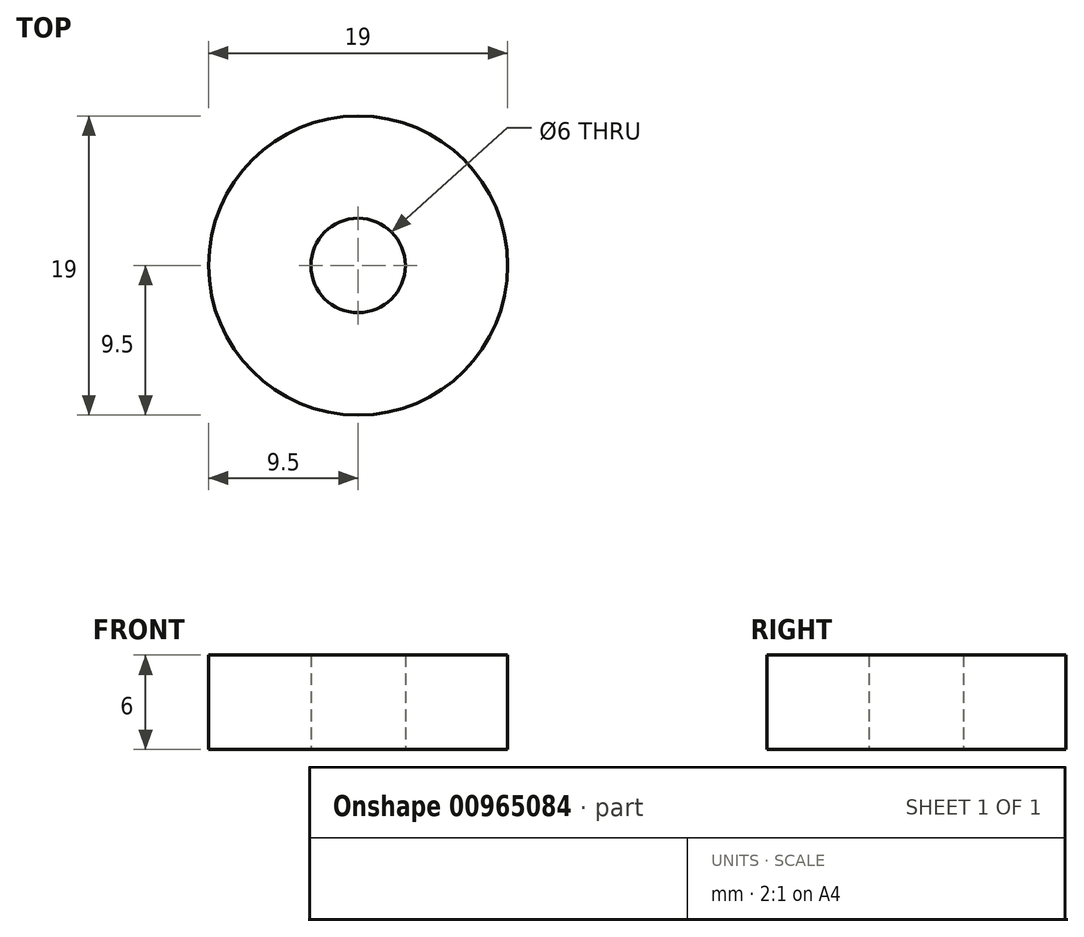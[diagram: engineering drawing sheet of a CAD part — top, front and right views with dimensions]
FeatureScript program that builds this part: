
annotation { "Feature Type Name" : "Feature", "Feature Type Description" : "" }
export const myFeature = defineFeature(function(context is Context, id is Id, definition is map)
    precondition{}
    {
        {
            var Q0;
            Q0=qCreatedBy(makeId("Top.planeOp"),FACE);
            var sketch = newSketch(context, id + "F0", { "sketchPlane" : qUnion([Q0])});
            skCircle(sketch, "E0", {"center": v(0, 0) * mm, "radius": 9.5 * mm});
            skCircle(sketch, "E1", {"center": v(0, 0) * mm, "radius": 3 * mm});
            skSolve(sketch);
        }
        {
            var Q0;
            Q0=makeQuery(id+"F0.imprint","IMPRINT",FACE,{"disambiguationData":[TD([[makeQuery(id+"F0.imprint","IMPRINT",EDGE,{"derivedFrom":sQuery(id+"F0.wireOp",EDGE,"E0")}),1.0]])]});
            extrude(context, id + "F1", {"entities" : qUnion([Q0]), "depth" : 6 * mm, "offsetDistance" : 25 * mm});
        }
    });
